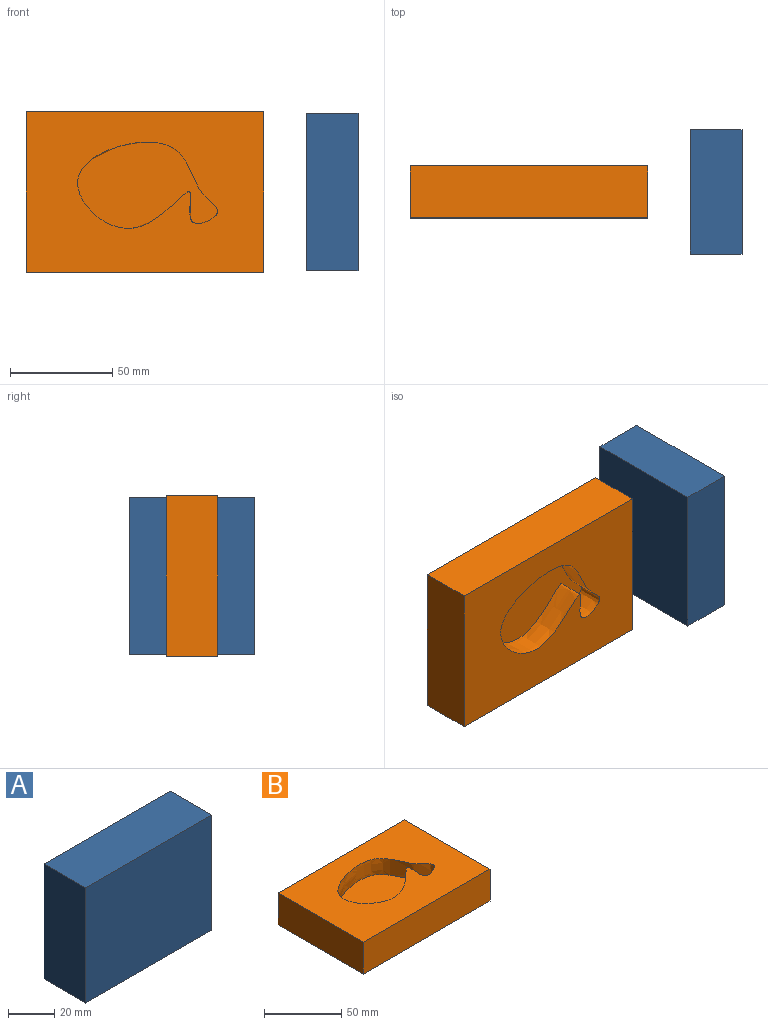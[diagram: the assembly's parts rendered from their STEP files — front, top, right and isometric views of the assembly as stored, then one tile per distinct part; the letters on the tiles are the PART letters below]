
ASSEMBLY  parts=2 mates=1
PART A: 6 faces, bbox 77.1x25.4x60.8 mm
  f0: plane 77.11x25.4mm, normal (0,0,1), area 1958.5mm2, adj f1,f3,f4,f5
  f1: plane 60.8x25.4mm, normal (-1,0,0), area 1544.4mm2, adj f0,f2,f4,f5
  f2: plane 77.11x25.4mm, normal (0,0,-1), area 1958.5mm2, adj f1,f3,f4,f5
  f3: plane 60.8x25.4mm, normal (1,0,0), area 1544.4mm2, adj f0,f2,f4,f5
  f4: plane 77.11x60.8mm, normal (0,-1,0), area 4688.3mm2, adj f0,f1,f2,f3
  f5: plane 77.11x60.8mm, normal (0,1,0), area 4688.3mm2, adj f0,f1,f2,f3
PART B: 8 faces, bbox 116.3x78.3x25.4 mm
  f0: plane 116.33x78.3mm, normal (0,0,1), area 7184.1mm2, adj f1,f2,f3,f4,f6
  f1: plane 78.3x25.4mm, normal (1,0,0), area 1988.9mm2, adj f0,f2,f4,f5
  f2: plane 116.33x25.4mm, normal (0,1,0), area 2954.7mm2, adj f0,f1,f3,f5
  f3: plane 78.3x25.4mm, normal (-1,0,0), area 1988.9mm2, adj f0,f2,f4,f5
  f4: plane 116.33x25.4mm, normal (0,-1,0), area 2954.7mm2, adj f0,f1,f3,f5
  f5: plane 116.33x78.3mm, normal (0,0,-1), area 9108.8mm2, adj f1,f2,f3,f4
  f6: extruded ~68.03x42.13mm, area 2505.9mm2, adj f0,f7
  f7: plane 72.7x46.61mm, normal (0,0,1), area 1924.3mm2, adj f6
PLACE A rot(axis=(0.58,0.58,-0.58),120deg) t=(119.77,46.78,53.45)mm
PLACE B rot(axis=(1,0,0),90deg) t=(15.52,59.48,53.45)mm
MATE slider A.f5 <-> B.f1  axis (1,0,0) through (119.77,46.78,53.45)mm
